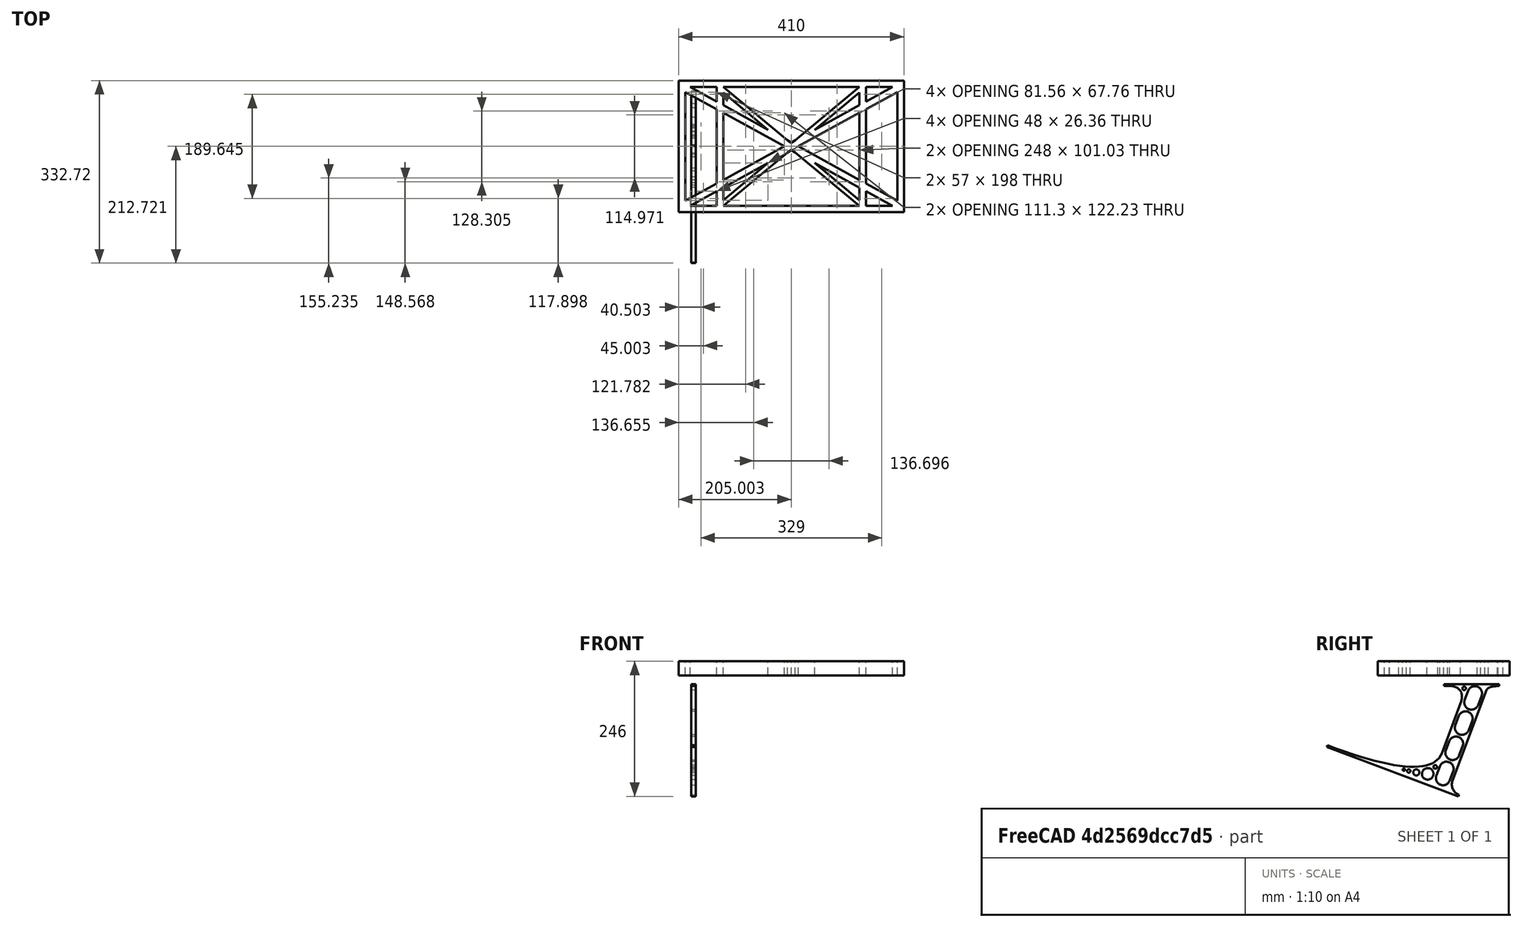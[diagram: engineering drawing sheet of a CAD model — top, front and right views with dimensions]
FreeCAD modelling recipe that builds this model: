
FCSTD DOCUMENT  (FreeCAD 0.19R0.19.2)
Label: laptopStand038
License: All rights reserved
LicenseURL: http://en.wikipedia.org/wiki/All_rights_reserved
objects: Sketcher::SketchObject×3, Part::Extrusion×2
note: 5 computed .brp shape members not serialized (recipe doc carries the construction recipe); baked Part::Feature solids carry a one-line shape summary decoded from their .brp

FEATURE [Sketcher::SketchObject] Sketch
  FullyConstrained = true
  sketch-geometry (52):
    g0: LineSegment StartX=-22.9272 StartY=136.221 StartZ=0 EndX=-22.9272 EndY=-103.779 EndZ=0
    g1: LineSegment StartX=-22.9272 StartY=136.221 StartZ=0 EndX=387.073 EndY=136.221 EndZ=0
    g2: LineSegment StartX=-22.9272 StartY=-103.779 StartZ=0 EndX=387.073 EndY=-103.779 EndZ=0
    g3: LineSegment StartX=387.073 StartY=136.221 StartZ=0 EndX=387.073 EndY=-103.779 EndZ=0
    g4: LineSegment StartX=375.073 StartY=115.221 StartZ=0 EndX=318.073 EndY=83.9235 EndZ=0
    g5: LineSegment StartX=-10.9272 StartY=-82.7794 StartZ=0 EndX=46.0728 EndY=-51.4823 EndZ=0
    g6: LineSegment StartX=-1.92719 StartY=124.221 StartZ=0 EndX=46.0728 EndY=97.8651 EndZ=0
    g7: LineSegment StartX=366.073 StartY=-91.7794 StartZ=0 EndX=318.073 EndY=-65.424 EndZ=0
    g8: LineSegment StartX=-10.9272 StartY=115.221 StartZ=0 EndX=-10.9272 EndY=-82.7794 EndZ=0
    g9: LineSegment StartX=375.073 StartY=-82.7794 StartZ=0 EndX=375.073 EndY=115.221 EndZ=0
    g10: LineSegment StartX=-1.92719 StartY=-91.7794 StartZ=0 EndX=46.0728 EndY=-91.7794 EndZ=0
    g11: LineSegment StartX=318.073 StartY=124.221 StartZ=0 EndX=366.073 EndY=124.221 EndZ=0
    g12: LineSegment StartX=306.073 StartY=-81.8102 StartZ=0 EndX=224.513 EndY=-14.0532 EndZ=0
    g13: LineSegment StartX=58.0728 StartY=114.251 StartZ=0 EndX=139.632 EndY=46.4944 EndZ=0
    g14: LineSegment StartX=306.073 StartY=124.221 StartZ=0 EndX=189.124 EndY=27.0628 EndZ=0
    g15: LineSegment StartX=58.0728 StartY=-91.7794 StartZ=0 EndX=175.022 EndY=5.37834 EndZ=0
    g16: LineSegment StartX=46.0728 StartY=124.221 StartZ=0 EndX=46.0728 EndY=97.8651 EndZ=0
    g17: LineSegment StartX=58.0728 StartY=-81.8102 StartZ=0 EndX=58.0728 EndY=-58.8351 EndZ=0
    g18: LineSegment StartX=318.073 StartY=124.221 StartZ=0 EndX=318.073 EndY=97.8651 EndZ=0
    g19: LineSegment StartX=306.073 StartY=114.251 StartZ=0 EndX=306.073 EndY=91.2763 EndZ=0
    g20: LineSegment StartX=182.073 StartY=23.1914 StartZ=0 EndX=189.124 EndY=27.0628 EndZ=0
    g21: LineSegment StartX=182.073 StartY=9.24976 StartZ=0 EndX=175.022 EndY=5.37834 EndZ=0
    g22: LineSegment StartX=224.513 StartY=46.4944 StartZ=0 EndX=306.073 EndY=114.251 EndZ=0
    g23: LineSegment StartX=175.022 StartY=27.0628 StartZ=0 EndX=58.0728 EndY=124.221 EndZ=0
    g24: LineSegment StartX=169.377 StartY=16.2206 StartZ=0 EndX=58.0728 EndY=77.3346 EndZ=0
    g25: LineSegment StartX=139.632 StartY=-14.0532 StartZ=0 EndX=58.0728 EndY=-81.8102 EndZ=0
    g26: LineSegment StartX=194.768 StartY=16.2206 StartZ=0 EndX=306.073 EndY=-44.8935 EndZ=0
    g27: LineSegment StartX=224.513 StartY=46.4944 StartZ=0 EndX=306.073 EndY=91.2763 EndZ=0
    g28: LineSegment StartX=175.022 StartY=27.0628 StartZ=0 EndX=182.073 EndY=23.1914 EndZ=0
    g29: LineSegment StartX=139.632 StartY=-14.0532 StartZ=0 EndX=58.0728 EndY=-58.8351 EndZ=0
    g30: LineSegment StartX=189.124 StartY=5.37834 StartZ=0 EndX=182.073 EndY=9.24976 EndZ=0
    g31: LineSegment StartX=189.124 StartY=5.37834 StartZ=0 EndX=306.073 EndY=-91.7794 EndZ=0
    g32: LineSegment StartX=306.073 StartY=77.3346 StartZ=0 EndX=306.073 EndY=-44.8935 EndZ=0
    g33: LineSegment StartX=318.073 StartY=83.9235 StartZ=0 EndX=318.073 EndY=-51.4823 EndZ=0
    g34: LineSegment StartX=318.073 StartY=97.8651 StartZ=0 EndX=366.073 EndY=124.221 EndZ=0
    g35: LineSegment StartX=306.073 StartY=77.3346 StartZ=0 EndX=194.768 EndY=16.2206 EndZ=0
    g36: LineSegment StartX=306.073 StartY=-58.8351 StartZ=0 EndX=224.513 EndY=-14.0532 EndZ=0
    g37: LineSegment StartX=306.073 StartY=-58.8351 StartZ=0 EndX=306.073 EndY=-81.8102 EndZ=0
    g38: LineSegment StartX=318.073 StartY=-51.4823 StartZ=0 EndX=375.073 EndY=-82.7794 EndZ=0
    g39: LineSegment StartX=318.073 StartY=-65.424 StartZ=0 EndX=318.073 EndY=-91.7794 EndZ=0
    g40: LineSegment StartX=306.073 StartY=124.221 StartZ=0 EndX=58.0728 EndY=124.221 EndZ=0
    g41: LineSegment StartX=318.073 StartY=-91.7794 StartZ=0 EndX=366.073 EndY=-91.7794 EndZ=0
    g42: LineSegment StartX=58.0728 StartY=-91.7794 StartZ=0 EndX=306.073 EndY=-91.7794 EndZ=0
    g43: LineSegment StartX=58.0728 StartY=-44.8935 StartZ=0 EndX=58.0728 EndY=77.3346 EndZ=0
    g44: LineSegment StartX=46.0728 StartY=-65.424 StartZ=0 EndX=-1.92719 EndY=-91.7794 EndZ=0
    g45: LineSegment StartX=46.0728 StartY=-65.424 StartZ=0 EndX=46.0728 EndY=-91.7794 EndZ=0
    g46: LineSegment StartX=58.0728 StartY=-44.8935 StartZ=0 EndX=169.377 EndY=16.2206 EndZ=0
    g47: LineSegment StartX=58.0728 StartY=91.2763 StartZ=0 EndX=58.0728 EndY=114.251 EndZ=0
    g48: LineSegment StartX=46.0728 StartY=83.9235 StartZ=0 EndX=46.0728 EndY=-51.4823 EndZ=0
    g49: LineSegment StartX=46.0728 StartY=124.221 StartZ=0 EndX=-1.92719 EndY=124.221 EndZ=0
    g50: LineSegment StartX=58.0728 StartY=91.2763 StartZ=0 EndX=139.632 EndY=46.4944 EndZ=0
    g51: LineSegment StartX=46.0728 StartY=83.9235 StartZ=0 EndX=-10.9272 EndY=115.221 EndZ=0
  constraints (102):
    c: Vertical(g0)
    c: Distance(g0) = 240
    c: Horizontal(g1)
    c: Distance(g1) = 410
    c: Coincident(g1,g0)
    c: Coincident(g2,g0)
    c: Horizontal(g2)
    c: Coincident(g3,g1)
    c: Vertical(g3)
    c: Coincident(g2,g3)
    c: Block(g1)
    c: Horizontal(g10)
    c: Horizontal(g11)
    c: PointOnObject(g35,g6)
    c: Coincident(g28,g20)
    c: Coincident(g30,g21)
    c: Tangent(g7,g24)
    c: PointOnObject(g24,g5)
    c: PointOnObject(g26,g4)
    c: Coincident(g20,g14)
    c: Tangent(g20,g27)
    c: Coincident(g50,g13)
    c: Coincident(g28,g23)
    c: Coincident(g22,g27)
    c: Coincident(g21,g15)
    c: Coincident(g29,g25)
    c: Tangent(g21,g29)
    c: Coincident(g36,g12)
    c: Coincident(g31,g30)
    c: Coincident(g22,g19)
    c: Tangent(g19,g32)
    c: Tangent(g18,g33)
    c: Coincident(g27,g19)
    c: Tangent(g27,g34)
    c: Coincident(g4,g33)
    c: Coincident(g35,g32)
    c: Tangent(g4,g35)
    c: Coincident(g37,g12)
    c: Tangent(g7,g36)
    c: Tangent(g32,g37)
    c: Coincident(g26,g32)
    c: Tangent(g26,g38)
    c: Coincident(g33,g38)
    c: Coincident(g39,g7)
    c: Tangent(g33,g39)
    c: Coincident(g25,g17)
    c: Tangent(g17,g43)
    c: Coincident(g29,g17)
    c: Tangent(g29,g44)
    c: Coincident(g45,g44)
    c: Tangent(g16,g45)
    c: Coincident(g5,g48)
    c: Coincident(g46,g43)
    c: Tangent(g5,g46)
    c: Tangent(g43,g47)
    c: Tangent(g16,g48)
    c: Coincident(g13,g47)
    c: PointOnObject(g40,g23)
    c: Tangent(g40,g49)
    c: Coincident(g6,g16)
    c: Coincident(g50,g47)
    c: Tangent(g6,g50)
    c: Coincident(g24,g43)
    c: Coincident(g51,g48)
    c: Tangent(g24,g51)
    c: Block(g23)
    c: Block(g14)
    c: Block(g20)
    c: Block(g40)
    c: Block(g18)
    c: Block(g34)
    c: Block(g4)
    c: Block(g38)
    c: Block(g9)
    c: Block(g36)
    c: Block(g37)
    c: Block(g7)
    c: Block(g39)
    c: Block(g22)
    c: Block(g31)
    c: Block(g42)
    c: Block(g21)
    c: Block(g15)
    c: Block(g29)
    c: Block(g25)
    c: Block(g45)
    c: Block(g44)
    c: Block(g5)
    c: Block(g8)
    c: Block(g51)
    c: Block(g6)
    c: Block(g16)
    c: Block(g13)
    c: Block(g47)
    c: Block(g35)
    c: Block(g32)
    c: Block(g24)
    c: Block(g46)
    c: Block(g49)
    c: Block(g11)
    c: Block(g41)
    c: Block(g10)
FEATURE [Part::Extrusion] Extrude
  Base = -> Sketch
  Dir = (0,0,1)
  DirMode = 2
  FaceMakerClass = Part::FaceMakerBullseye
  LengthFwd = 26
  LengthRev = 0
  Solid = true
  Symmetric = false
FEATURE [Sketcher::SketchObject] Sketch001
  FullyConstrained = true
  MapMode = 4
  Placement = pos=(0,0,0) rot=(0.57735,0.57735,0.57735;2.0944rad)
  Support = -> [Sketch]
  sketch-geometry (46):
    g0: BSplineCurve PolesCount=3 KnotsCount=2 Degree=2 IsPeriodic=0
    g1: ArcOfCircle CenterX=73.122 CenterY=-32.2909 CenterZ=0 NormalX=0 NormalY=0 NormalZ=1 AngleXU=0 Radius=13 StartAngle=5.92268 EndAngle=9.06428
    g2: ArcOfCircle CenterX=66.7816 CenterY=-49.1439 CenterZ=0 NormalX=0 NormalY=0 NormalZ=1 AngleXU=0 Radius=13 StartAngle=2.78068 EndAngle=5.92131
    g3: ArcOfCircle CenterX=55.9263 CenterY=-78.1807 CenterZ=0 NormalX=0 NormalY=0 NormalZ=1 AngleXU=0 Radius=13 StartAngle=5.92268 EndAngle=9.06428
    g4: ArcOfCircle CenterX=49.5884 CenterY=-95.0342 CenterZ=0 NormalX=0 NormalY=0 NormalZ=1 AngleXU=0 Radius=13 StartAngle=2.78068 EndAngle=5.92131
    g5: ArcOfCircle CenterX=38.7206 CenterY=-124.067 CenterZ=0 NormalX=0 NormalY=0 NormalZ=1 AngleXU=0 Radius=13 StartAngle=5.92268 EndAngle=9.06428
    g6: ArcOfCircle CenterX=32.3875 CenterY=-140.92 CenterZ=0 NormalX=0 NormalY=0 NormalZ=1 AngleXU=0 Radius=13 StartAngle=2.78068 EndAngle=5.92131
    g7: ArcOfCircle CenterX=21.4715 CenterY=-169.934 CenterZ=0 NormalX=0 NormalY=0 NormalZ=1 AngleXU=0 Radius=13 StartAngle=5.92268 EndAngle=9.06428
    g8: ArcOfCircle CenterX=15.1336 CenterY=-186.787 CenterZ=0 NormalX=0 NormalY=0 NormalZ=1 AngleXU=0 Radius=13 StartAngle=2.78068 EndAngle=5.92131
    g9-g12: Circle x4 (B-spline internal-alignment scaffolding for g13; pole/knot coordinates omitted)
    g13: BSplineCurve PolesCount=4 KnotsCount=2 Degree=3 IsPeriodic=0
    g14: GeomPoint X=28.8094 Y=-19.0875 Z=0
    g15: GeomPoint X=47.0443 Y=-50.4712 Z=0
    g16: Circle CenterX=53.5586 CenterY=-23.2695 CenterZ=0 NormalX=0 NormalY=0 NormalZ=1 AngleXU=0 Radius=3.24518
    g17: Circle CenterX=-195.441 CenterY=-127.082 CenterZ=0 NormalX=0 NormalY=0 NormalZ=1 AngleXU=0 Radius=1
    g18: Circle CenterX=-8.24091 CenterY=-197.481 CenterZ=0 NormalX=0 NormalY=0 NormalZ=1 AngleXU=0 Radius=1
    g19: Circle CenterX=12.8789 CenterY=-141.321 CenterZ=0 NormalX=0 NormalY=0 NormalZ=1 AngleXU=0 Radius=1
    g20: BSplineCurve PolesCount=3 KnotsCount=2 Degree=2 IsPeriodic=0
    g21: GeomPoint X=-195.441 Y=-127.082 Z=0
    g22: GeomPoint X=12.8789 Y=-141.321 Z=0
    g23: Circle CenterX=-12.8016 CenterY=-179.036 CenterZ=0 NormalX=0 NormalY=0 NormalZ=1 AngleXU=0 Radius=10.5072
    g24: Circle CenterX=0.933922 CenterY=-166.43 CenterZ=0 NormalX=0 NormalY=0 NormalZ=1 AngleXU=0 Radius=3.26661
    g25: Circle CenterX=-33.5518 CenterY=-176.44 CenterZ=0 NormalX=0 NormalY=0 NormalZ=1 AngleXU=0 Radius=5.64388
    g26: Circle CenterX=-47.2366 CenterY=-173.859 CenterZ=0 NormalX=0 NormalY=0 NormalZ=1 AngleXU=0 Radius=3.01653
    g27: Circle CenterX=-56.2595 CenterY=-171.456 CenterZ=0 NormalX=0 NormalY=0 NormalZ=1 AngleXU=0 Radius=2.12826
    g28: ArcOfCircle CenterX=51.2151 CenterY=-198.473 CenterZ=0 NormalX=0 NormalY=0 NormalZ=1 AngleXU=0 Radius=20 StartAngle=2.78189 EndAngle=4.35269
    g29: LineSegment StartX=32.4951 StartY=-191.433 StartZ=0 EndX=94.6577 EndY=-26.1351 EndZ=0
    g30: LineSegment StartX=43.1192 StartY=-220.001 StartZ=0 EndX=-196.497 EndY=-129.89 EndZ=0
    g31: LineSegment StartX=43.1192 StartY=-220.001 StartZ=0 EndX=44.1752 EndY=-217.193 EndZ=0
    g32: LineSegment StartX=117.223 StartY=-19.0875 StartZ=0 EndX=117.223 EndY=-16.0875 EndZ=0
    g33: LineSegment StartX=117.223 StartY=-16.0875 StartZ=0 EndX=17.2232 EndY=-16.0875 EndZ=0
    g34: LineSegment StartX=17.2232 StartY=-16.0875 StartZ=0 EndX=17.2232 EndY=-19.0875 EndZ=0
    g35: LineSegment StartX=28.8094 StartY=-19.0875 StartZ=0 EndX=17.2232 EndY=-19.0875 EndZ=0
    g36: LineSegment StartX=47.0443 StartY=-50.4712 StartZ=0 EndX=12.8789 EndY=-141.321 EndZ=0
    g37: LineSegment StartX=-195.441 StartY=-127.082 StartZ=0 EndX=-196.497 EndY=-129.89 EndZ=0
    g38: LineSegment StartX=85.2864 StartY=-36.8765 StartZ=0 EndX=78.9396 EndY=-53.7463 EndZ=0
    g39: LineSegment StartX=60.9577 StartY=-27.7052 StartZ=0 EndX=54.6191 EndY=-44.5532 EndZ=0
    g40: LineSegment StartX=68.0907 StartY=-82.7664 StartZ=0 EndX=61.7465 EndY=-99.6365 EndZ=0
    g41: LineSegment StartX=43.7619 StartY=-73.595 StartZ=0 EndX=37.426 EndY=-90.4435 EndZ=0
    g42: LineSegment StartX=50.885 StartY=-128.652 StartZ=0 EndX=44.5456 EndY=-145.522 EndZ=0
    g43: LineSegment StartX=26.5562 StartY=-119.481 StartZ=0 EndX=20.2251 EndY=-136.329 EndZ=0
    g44: LineSegment StartX=9.3071 StartY=-165.349 StartZ=0 EndX=2.97115 EndY=-182.197 EndZ=0
    g45: LineSegment StartX=33.6358 StartY=-174.52 StartZ=0 EndX=27.2917 EndY=-191.39 EndZ=0
  constraints (70):
    c: Block(g0)
    c: Block(g1)
    c: Block(g2)
    c: Block(g4)
    c: Block(g3)
    c: Block(g6)
    c: Block(g5)
    c: Block(g8)
    c: Block(g7)
    c: Weight(g9) = 1
    c: Equal(g9,g10)
    c: Equal(g9,g11)
    c: Equal(g9,g12)
    c: InternalAlignment(g9-g12 -> g13) x4
    c: InternalAlignment(g14,g13)
    c: InternalAlignment(g15,g13)
    c: Block(g16)
    c: Weight(g17) = 1
    c: Equal(g17,g18)
    c: Equal(g17,g19)
    c: InternalAlignment(g17,g20)
    c: InternalAlignment(g18,g20)
    c: InternalAlignment(g19,g20)
    c: InternalAlignment(g21,g20)
    c: InternalAlignment(g22,g20)
    c: Block(g20)
    c: Block(g23)
    c: Block(g24)
    c: Block(g25)
    c: Block(g26)
    c: Block(g27)
    c: Block(g28)
    c: Coincident(g29,g28)
    c: Coincident(g29,g0)
    c: Block(g13)
    c: Coincident(g31,g30)
    c: Coincident(g31,g28)
    c: Block(g31)
    c: Coincident(g32,g0)
    c: Vertical(g32)
    c: Coincident(g33,g32)
    c: Horizontal(g33)
    c: Coincident(g34,g33)
    c: Vertical(g34)
    c: Block(g33)
    c: Coincident(g35,g13)
    c: Coincident(g35,g34)
    c: Horizontal(g35)
    c: Coincident(g36,g13)
    c: Coincident(g36,g20)
    c: Coincident(g37,g20)
    c: Coincident(g37,g30)
    c: Block(g30)
    c: Coincident(g38,g1)
    c: Coincident(g38,g2)
    c: Coincident(g39,g1)
    c: Coincident(g39,g2)
    c: Coincident(g40,g3)
    c: Coincident(g40,g4)
    c: Coincident(g41,g3)
    c: Coincident(g41,g4)
    c: Coincident(g42,g5)
    c: Coincident(g42,g6)
    c: Coincident(g43,g5)
    c: Coincident(g43,g6)
    c: Coincident(g44,g7)
    c: Coincident(g44,g8)
    c: Coincident(g45,g7)
    c: Coincident(g45,g8)
    c: Distance(g30) = 256
FEATURE [Part::Extrusion] Extrude002
  Base = -> Sketch001
  Dir = (1,0,0)
  DirMode = 2
  FaceMakerClass = Part::FaceMakerBullseye
  LengthFwd = 8
  LengthRev = 0
  Solid = true
  Symmetric = false
FEATURE [Sketcher::SketchObject] Sketch002
  FullyConstrained = false
  sketch-geometry (10):
    g0: LineSegment StartX=-2.26129 StartY=-200.425 StartZ=0 EndX=5.73871 EndY=-200.425 EndZ=0
    g1: LineSegment StartX=5.73871 StartY=-200.425 StartZ=0 EndX=5.73871 EndY=-197.425 EndZ=0
    g2: LineSegment StartX=-2.26129 StartY=-200.425 StartZ=0 EndX=-2.26129 EndY=-197.425 EndZ=0
    g3: LineSegment StartX=5.73871 StartY=-200.425 StartZ=0 EndX=5.73871 EndY=-206.425 EndZ=0
    g4: LineSegment StartX=-2.26129 StartY=-200.425 StartZ=0 EndX=-2.26129 EndY=-206.425 EndZ=0
    g5: LineSegment StartX=5.73871 StartY=-206.425 StartZ=0 EndX=19.7387 EndY=-206.425 EndZ=0
    g6: LineSegment StartX=-2.26129 StartY=-206.425 StartZ=0 EndX=-16.2613 EndY=-206.425 EndZ=0
    g7: LineSegment StartX=19.7387 StartY=-206.425 StartZ=0 EndX=19.7387 EndY=-209.425 EndZ=0
    g8: LineSegment StartX=-16.2613 StartY=-206.425 StartZ=0 EndX=-16.2613 EndY=-209.425 EndZ=0
    g9: LineSegment StartX=-16.2613 StartY=-209.425 StartZ=0 EndX=19.7387 EndY=-209.425 EndZ=0
  constraints (28):
    c: Horizontal(g0)
    c: Distance(g0) = 8
    c: Coincident(g1,g0)
    c: Vertical(g1)
    c: Distance(g1) = 3
    c: Coincident(g2,g0)
    c: Vertical(g2)
    c: Distance(g2) = 3
    c: Coincident(g3,g0)
    c: Vertical(g3)
    c: Distance(g3) = 6
    c: Coincident(g4,g0)
    c: Vertical(g4)
    c: Distance(g4) = 6
    c: Coincident(g5,g3)
    c: Horizontal(g5)
    c: Distance(g5) = 14
    c: Coincident(g6,g4)
    c: Horizontal(g6)
    c: Distance(g6) = 14
    c: Coincident(g7,g5)
    c: Vertical(g7)
    c: Distance(g7) = 3
    c: Coincident(g8,g6)
    c: Vertical(g8)
    c: Distance(g8) = 3
    c: Coincident(g9,g8)
    c: Coincident(g9,g7)
